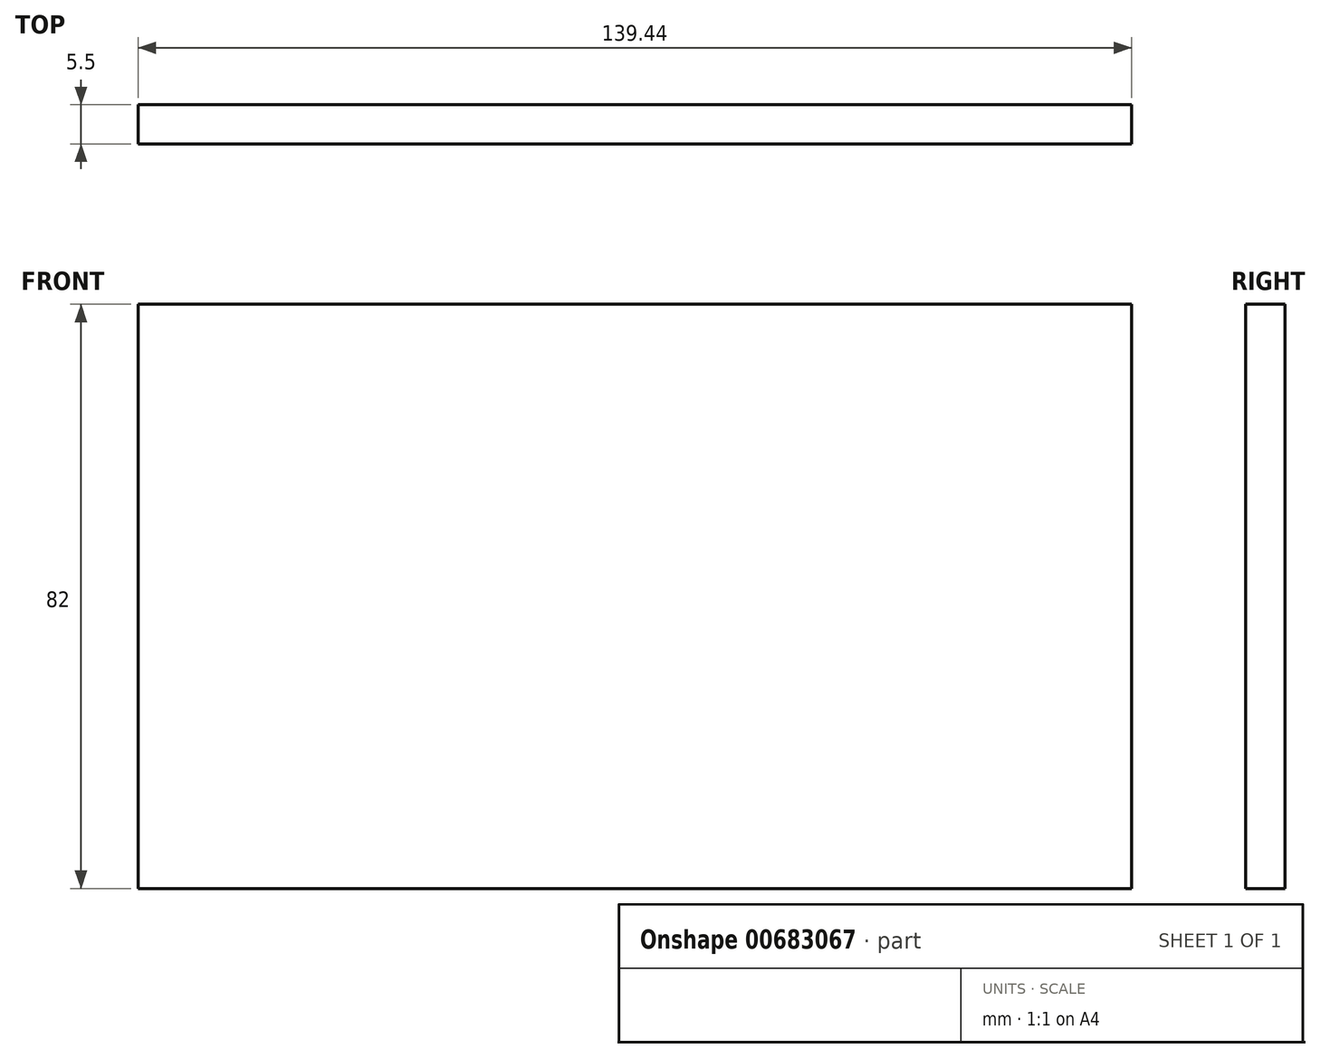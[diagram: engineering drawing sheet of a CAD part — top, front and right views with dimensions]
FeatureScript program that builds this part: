
annotation { "Feature Type Name" : "Feature", "Feature Type Description" : "" }
export const myFeature = defineFeature(function(context is Context, id is Id, definition is map)
    precondition{}
    {
        {
            var Q0;
            Q0=qCreatedBy(makeId("Top.planeOp"),FACE);
            var sketch = newSketch(context, id + "F0", { "sketchPlane" : qUnion([Q0])});
            skLineSegment(sketch, "E0.bottom", {"start": v(69.72, -2.75) * mm, "end": v(-69.72, -2.75) * mm});
            skLineSegment(sketch, "E0.top", {"start": v(69.72, 2.75) * mm, "end": v(-69.72, 2.75) * mm});
            skLineSegment(sketch, "E0.left", {"start": v(69.72, -2.75) * mm, "end": v(69.72, 2.75) * mm});
            skLineSegment(sketch, "E0.right", {"start": v(-69.72, -2.75) * mm, "end": v(-69.72, 2.75) * mm});
            skPoint(sketch, "E0.middle", {"position": v(0, 0) * mm});
            skSolve(sketch);
        }
        {
            var Q0;
            Q0=makeQuery(id+"F0.imprint","IMPRINT",FACE,{"disambiguationData":[TD([[makeQuery(id+"F0.imprint","IMPRINT",EDGE,{"derivedFrom":sQuery(id+"F0.wireOp",EDGE,"E0.bottom")}),-1.0]])]});
            extrude(context, id + "F1", {"entities" : qUnion([Q0]), "depth" : 82 * mm, "offsetDistance" : 25 * mm});
        }
    });
